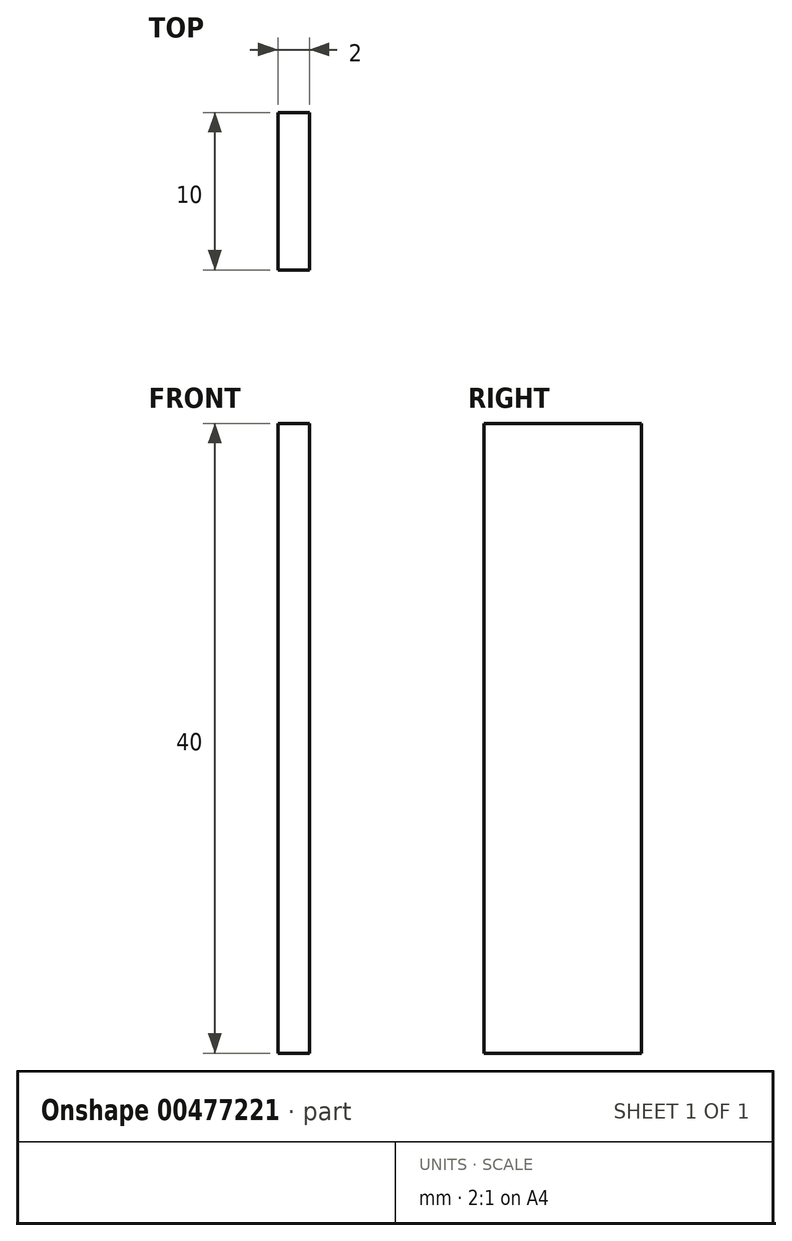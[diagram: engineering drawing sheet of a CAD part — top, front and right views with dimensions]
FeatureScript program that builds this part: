
annotation { "Feature Type Name" : "Feature", "Feature Type Description" : "" }
export const myFeature = defineFeature(function(context is Context, id is Id, definition is map)
    precondition{}
    {
        {
            var Q0;
            Q0=qCreatedBy(makeId("Right.planeOp"),FACE);
            var sketch = newSketch(context, id + "F0", { "sketchPlane" : qUnion([Q0])});
            skLineSegment(sketch, "E0", {"start": v(0, 0) * mm, "end": v(-25, 0) * mm});
            skLineSegment(sketch, "E1.bottom", {"start": v(-25, 0) * mm, "end": v(-35, 0) * mm});
            skLineSegment(sketch, "E1.top", {"start": v(-25, 40) * mm, "end": v(-35, 40) * mm});
            skLineSegment(sketch, "E1.left", {"start": v(-25, 0) * mm, "end": v(-25, 40) * mm});
            skLineSegment(sketch, "E1.right", {"start": v(-35, 0) * mm, "end": v(-35, 40) * mm});
            skSolve(sketch);
        }
        {
            var Q0;
            Q0=qSketchRegion(id+"F0",true);
            extrude(context, id + "F1", {"entities" : qUnion([Q0]), "endBound" : BoundingType.SYMMETRIC, "depth" : 2 * mm});
        }
    });
